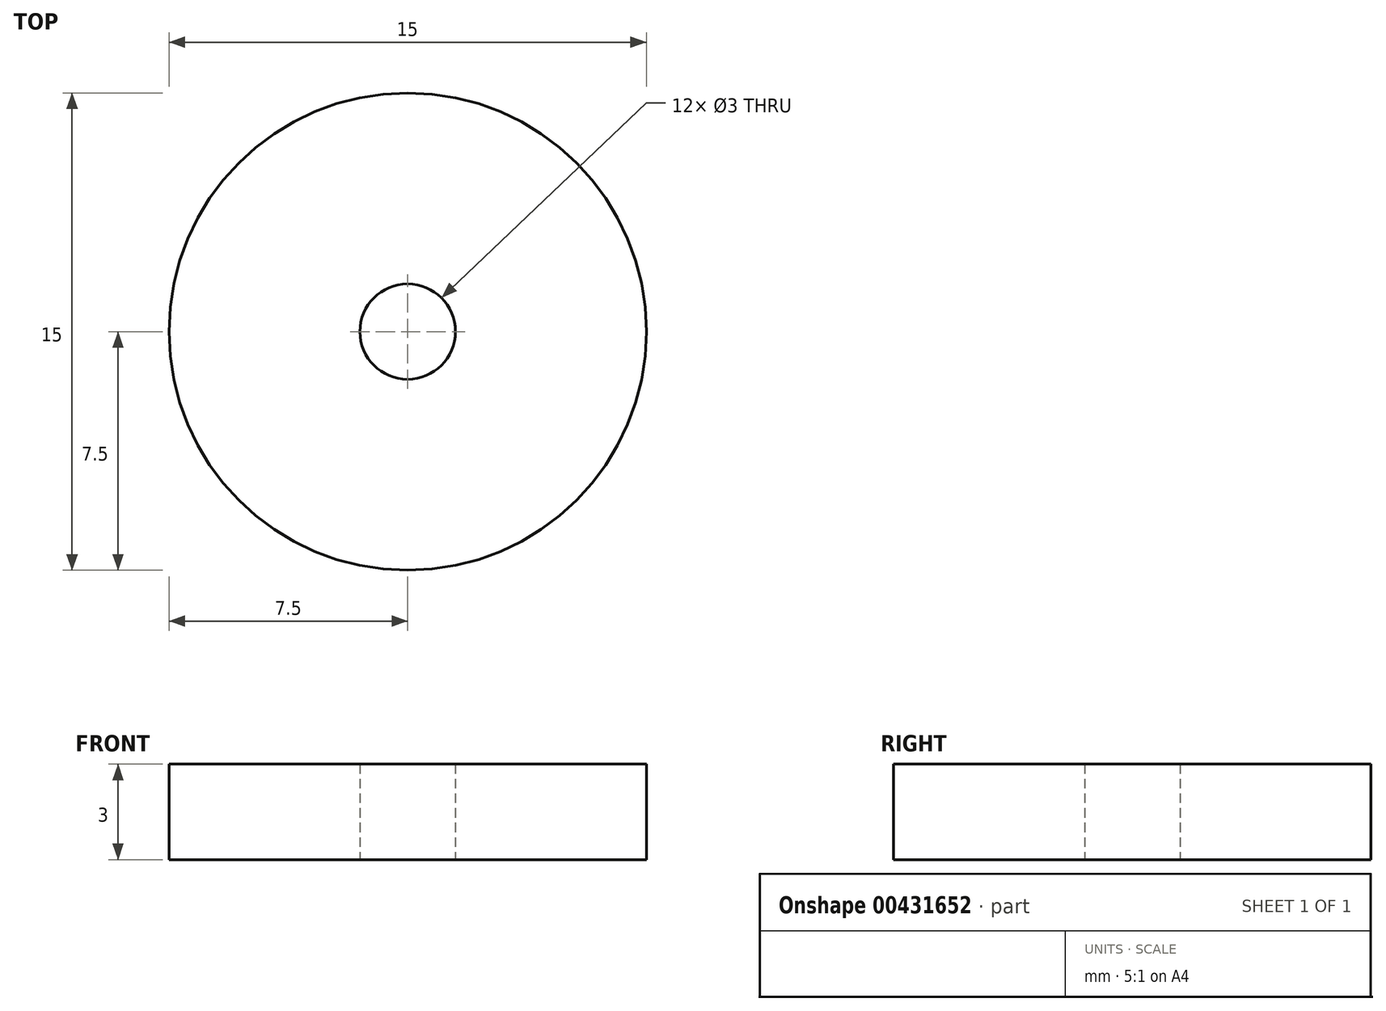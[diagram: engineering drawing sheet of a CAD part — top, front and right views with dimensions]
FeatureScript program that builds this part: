
annotation { "Feature Type Name" : "Feature", "Feature Type Description" : "" }
export const myFeature = defineFeature(function(context is Context, id is Id, definition is map)
    precondition{}
    {
        {
            var Q0;
            Q0=qCreatedBy(makeId("Top.planeOp"),FACE);
            var sketch = newSketch(context, id + "F0", { "sketchPlane" : qUnion([Q0])});
            skCircle(sketch, "E0", {"center": v(0, 0) * mm, "radius": 7.5 * mm});
            skLineSegment(sketch, "E1", {"start": v(0, 0) * mm, "end": v(0, 12.2) * mm});
            skLineSegment(sketch, "E2", {"start": v(0, 7.5) * mm, "end": v(0, 10) * mm});
            skLineSegment(sketch, "E3", {"start": v(0, 10) * mm, "end": v(-1.5, 10) * mm, "construction": true});
            skLineSegment(sketch, "E4", {"start": v(-1.5, 10) * mm, "end": v(1.5, 10) * mm, "construction": true});
            skPoint(sketch, "E4.endSnap0", {"position": v(-0.75, 10) * mm});
            skLineSegment(sketch, "E5", {"start": v(0, 7.5) * mm, "end": v(-2, 7.5) * mm, "construction": true});
            skLineSegment(sketch, "E6", {"start": v(-2, 7.5) * mm, "end": v(2, 7.5) * mm, "construction": true});
            skLineSegment(sketch, "E7", {"start": v(2, 7.5) * mm, "end": v(2, 7.23) * mm, "construction": true});
            skLineSegment(sketch, "E8", {"start": v(-2, 7.5) * mm, "end": v(-2, 7.23) * mm, "construction": true});
            skFitSpline(sketch, "E9", {"points": [v(-2, 7.23) * mm, v(-1.5, 10) * mm, v(0, 12.2) * mm, v(1.5, 10) * mm, v(2, 7.23) * mm], "startDerivative": vector(0.94, 10.32) * mm, "endDerivative": vector(0.84, -10.8) * mm});
            skCircle(sketch, "E10", {"center": v(0, 0) * mm, "radius": 1.5 * mm});
            skSolve(sketch);
        }
        {
            var Q0;
            {var subQ0=sQuery(id+"F0.wireOp",EDGE,"E0");var subQ1=makeQuery(id+"F0.imprint","INTERSECT",VERTEX,{"derivedFrom":[subQ0,sQuery(id+"F0.wireOp",EDGE,"E2")]});Q0=makeQuery(id+"F0.imprint","IMPRINT",FACE,{"disambiguationData":[TD([[makeQuery(id+"F0.imprint","IMPRINT",EDGE,{"disambiguationData":[TD([[subQ1,1.0]])],"derivedFrom":subQ0}),1.0]])]});}
            var Q1;
            {var subQ0=sQuery(id+"F0.wireOp",EDGE,"E2");Q1=makeQuery(id+"F0.imprint","IMPRINT",FACE,{"disambiguationData":[TD([[makeQuery(id+"F0.imprint","IMPRINT",EDGE,{"derivedFrom":subQ0}),1.0]])]});}
            var Q2;
            {var subQ0=sQuery(id+"F0.wireOp",EDGE,"E2");Q2=makeQuery(id+"F0.imprint","IMPRINT",FACE,{"disambiguationData":[TD([[makeQuery(id+"F0.imprint","IMPRINT",EDGE,{"derivedFrom":subQ0}),-1.0]])]});}
            extrude(context, id + "F1", {"entities" : qUnion([Q0, Q1, Q2]), "depth" : 3 * mm});
        }
        {
            var Q0;
            Q0=makeQuery(id+"F1.opExtrude","SWEPT_BODY",BODY,{"disambiguationData":[OSD([sQuery(id+"F0.wireOp",EDGE,"E0"),sQuery(id+"F0.wireOp",EDGE,"E9"),sQuery(id+"F0.wireOp",EDGE,"E10")])]});
            var Q1;
            Q1=makeQuery(id+"F1.opExtrude","CAP_EDGE",EDGE,{"disambiguationData":[OSD([sQuery(id+"F0.wireOp",EDGE,"E10")])],"isStart":false});
            circularPattern(context, id + "F2", {"entities" : qUnion([Q0]), "axis" : qUnion([Q1]), "angle" : 360 * degree, "instanceCount" : 12, "equalSpace" : true});
        }
    });
